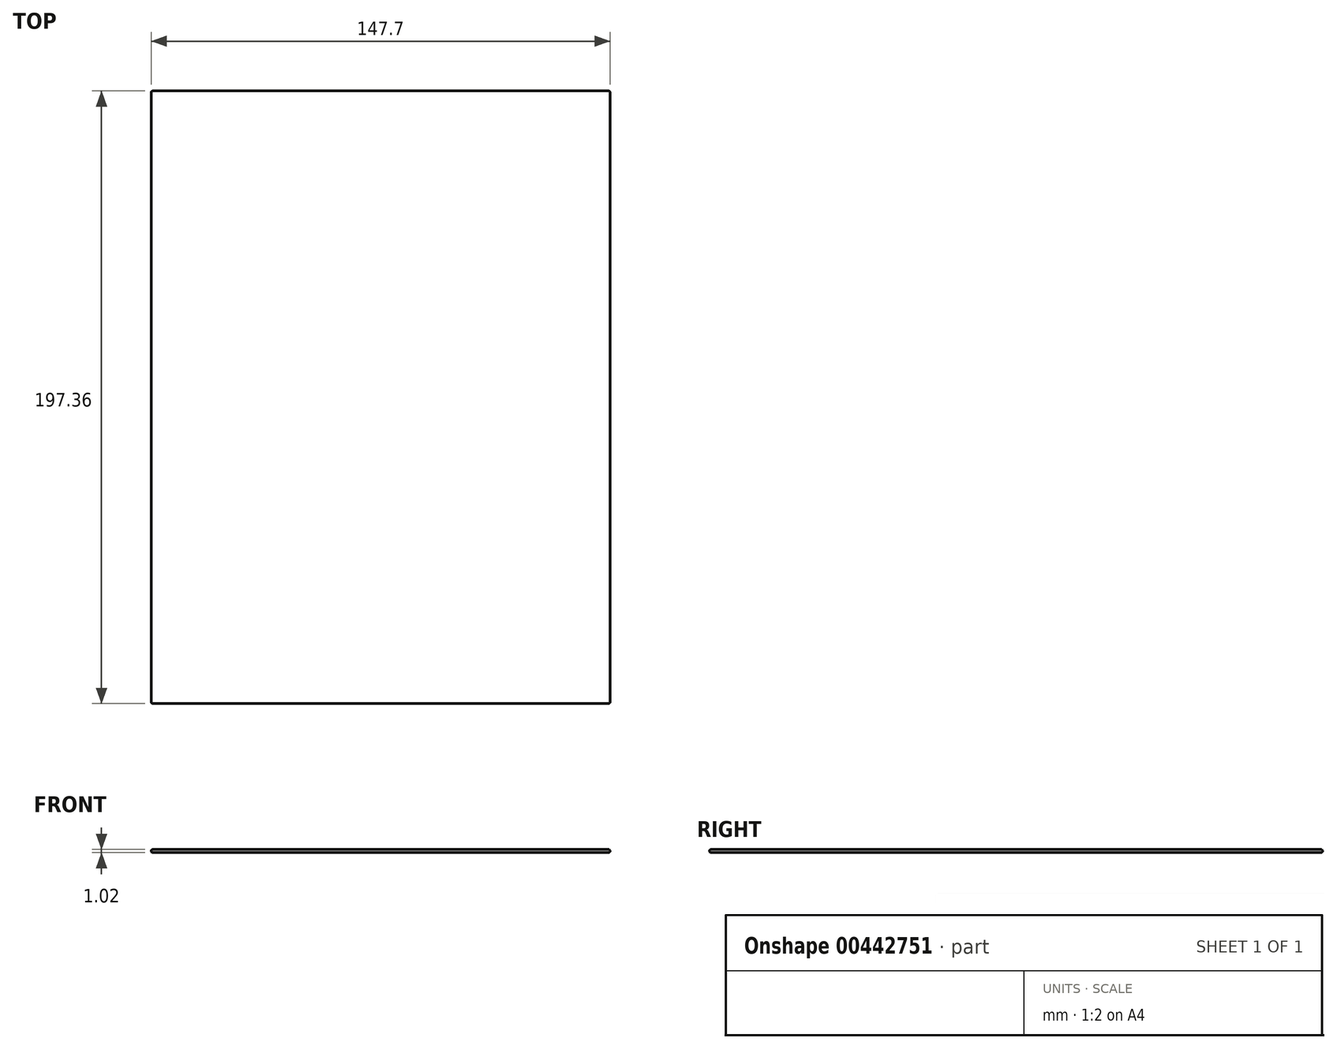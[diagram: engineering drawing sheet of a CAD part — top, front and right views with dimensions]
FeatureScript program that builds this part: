
annotation { "Feature Type Name" : "Feature", "Feature Type Description" : "" }
export const myFeature = defineFeature(function(context is Context, id is Id, definition is map)
    precondition{}
    {
        {
            var Q0;
            Q0=qCreatedBy(makeId("Top.planeOp"),FACE);
            var sketch = newSketch(context, id + "F0", { "sketchPlane" : qUnion([Q0])});
            skLineSegment(sketch, "E0.bottom", {"start": v(73.85, 98.68) * mm, "end": v(-73.85, 98.68) * mm});
            skLineSegment(sketch, "E0.top", {"start": v(73.85, -98.68) * mm, "end": v(-73.85, -98.68) * mm});
            skLineSegment(sketch, "E0.left", {"start": v(73.85, 98.68) * mm, "end": v(73.85, -98.68) * mm});
            skLineSegment(sketch, "E0.right", {"start": v(-73.85, 98.68) * mm, "end": v(-73.85, -98.68) * mm});
            skPoint(sketch, "E0.middle", {"position": v(0, 0) * mm});
            skSolve(sketch);
        }
        {
            var Q0;
            Q0 = qSketchRegion(id + "F0", true);
            extrude(context, id + "F1", {"entities" : qUnion([Q0]), "depth" : 1.02 * mm, "offsetDistance" : 25.4 * mm});
        }
        {
            var Q0;
            Q0=makeQuery(id+"F1.opExtrude","SWEPT_FACE",FACE,{"disambiguationData":[OSD([sQuery(id+"F0.wireOp",EDGE,"E0.left")])]});
            var Q1;
            Q1=makeQuery(id+"F1.opExtrude","SWEPT_FACE",FACE,{"disambiguationData":[OSD([sQuery(id+"F0.wireOp",EDGE,"E0.bottom")])]});
            var Q2;
            Q2=makeQuery(id+"F1.opExtrude","SWEPT_FACE",FACE,{"disambiguationData":[OSD([sQuery(id+"F0.wireOp",EDGE,"E0.right")])]});
            var Q3;
            Q3=makeQuery(id+"F1.opExtrude","SWEPT_FACE",FACE,{"disambiguationData":[OSD([sQuery(id+"F0.wireOp",EDGE,"E0.top")])]});
            fillet(context, id + "F2", {"entities" : qUnion([Q0, Q1, Q2, Q3]), "radius" : 0.5 * mm, "tangentPropagation" : true, "allowEdgeOverflow" : false});
        }
    });
